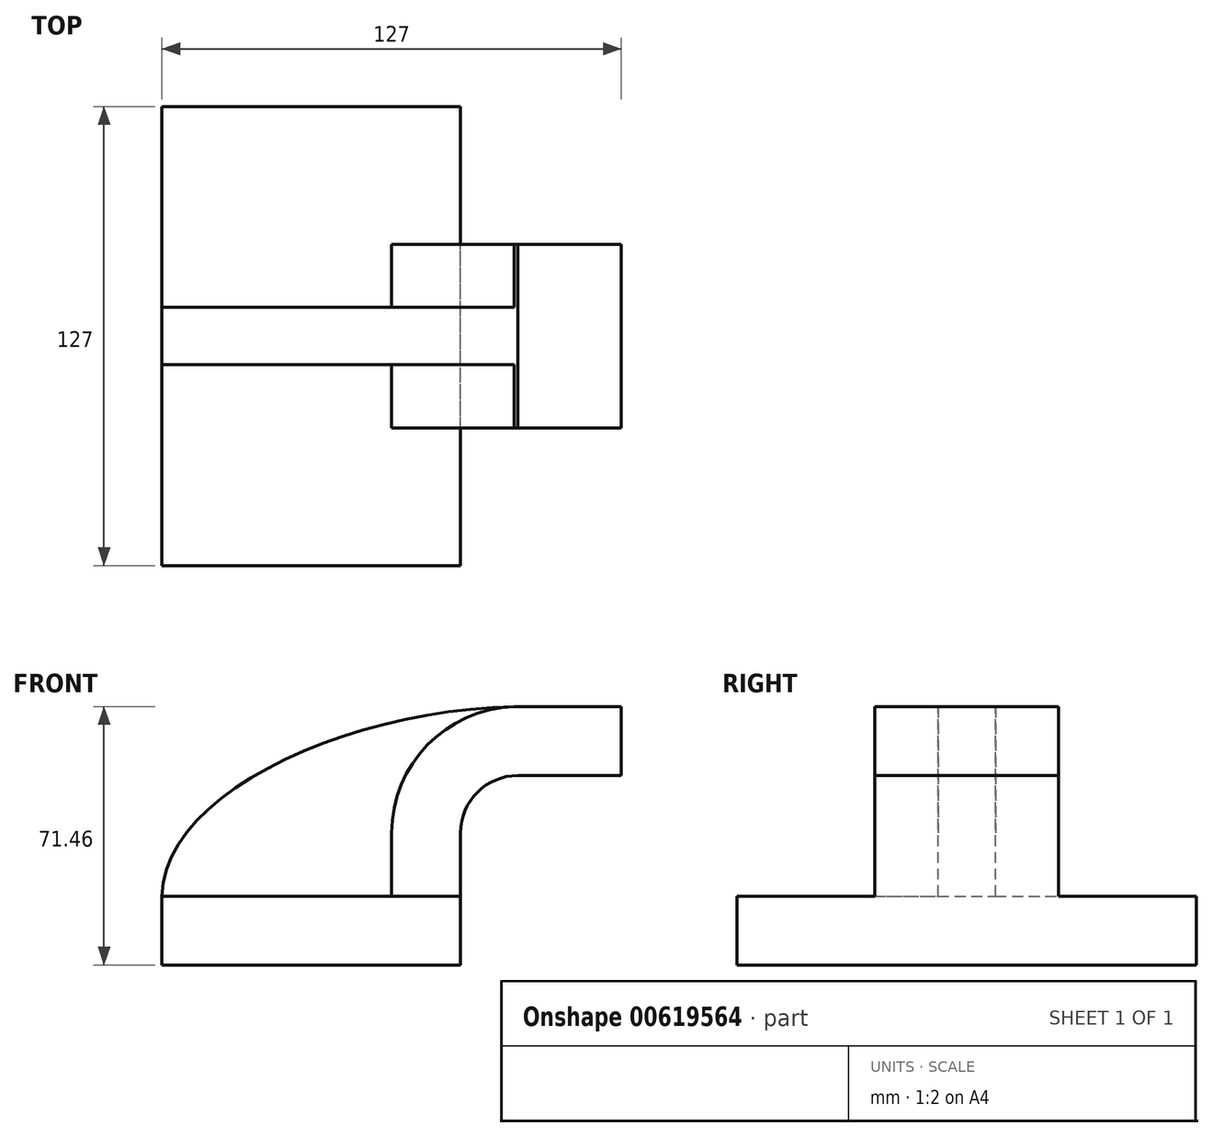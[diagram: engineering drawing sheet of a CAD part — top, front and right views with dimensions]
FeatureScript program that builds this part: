
annotation { "Feature Type Name" : "Feature", "Feature Type Description" : "" }
export const myFeature = defineFeature(function(context is Context, id is Id, definition is map)
    precondition{}
    {
        {
            var Q0;
            Q0=qCreatedBy(makeId("Front.planeOp"),FACE);
            var sketch = newSketch(context, id + "F0", { "sketchPlane" : qUnion([Q0])});
            skLineSegment(sketch, "E0.bottom", {"start": v(-41.28, -9.53) * mm, "end": v(41.28, -9.53) * mm});
            skLineSegment(sketch, "E0.top", {"start": v(-41.28, 9.53) * mm, "end": v(41.28, 9.53) * mm});
            skLineSegment(sketch, "E0.left", {"start": v(-41.28, -9.53) * mm, "end": v(-41.28, 9.53) * mm});
            skLineSegment(sketch, "E0.right", {"start": v(41.28, -9.53) * mm, "end": v(41.28, 9.53) * mm});
            skPoint(sketch, "E0.middle", {"position": v(0, 0) * mm});
            skLineSegment(sketch, "E1.bottom", {"start": v(60.32, 66.67) * mm, "end": v(111.12, 66.67) * mm});
            skLineSegment(sketch, "E1.top", {"start": v(60.32, 38.1) * mm, "end": v(111.12, 38.1) * mm});
            skLineSegment(sketch, "E1.left", {"start": v(60.32, 66.67) * mm, "end": v(60.32, 38.1) * mm});
            skLineSegment(sketch, "E1.right", {"start": v(111.12, 66.67) * mm, "end": v(111.12, 38.1) * mm});
            skPoint(sketch, "E1.middle", {"position": v(85.72, 52.39) * mm});
            skLineSegment(sketch, "E2", {"start": v(41.28, 9.53) * mm, "end": v(41.28, 27) * mm});
            skArc(sketch, "E3", {"start": v(41.28, 27) * mm, "mid": v(45.92, 38.23) * mm, "end": v(57.15, 42.88) * mm});
            skLineSegment(sketch, "E4", {"start": v(57.15, 42.88) * mm, "end": v(85.72, 42.88) * mm});
            skPoint(sketch, "E4.endSnap0", {"position": v(85.72, 38.1) * mm});
            skLineSegment(sketch, "E5.0", {"start": v(57.15, 61.93) * mm, "end": v(85.72, 61.93) * mm});
            skArc(sketch, "E5.1", {"start": v(22.23, 27) * mm, "mid": v(32.45, 51.7) * mm, "end": v(57.15, 61.93) * mm});
            skLineSegment(sketch, "E5.2", {"start": v(22.23, 9.53) * mm, "end": v(22.23, 27) * mm});
            skLineSegment(sketch, "E6", {"start": v(85.72, 42.88) * mm, "end": v(85.72, 66.67) * mm});
            skFitSpline(sketch, "E7", {"points": [v(-41.28, 9.53) * mm, v(57.15, 61.93) * mm], "startDerivative": vector(1.35, 85.95) * mm, "endDerivative": vector(139.55, 1.51) * mm});
            skSolve(sketch);
        }
        {
            var Q0;
            Q0=makeQuery(id+"F0.imprint","IMPRINT",FACE,{"disambiguationData":[TD([[makeQuery(id+"F0.imprint","IMPRINT",EDGE,{"derivedFrom":sQuery(id+"F0.wireOp",EDGE,"E0.bottom")}),1.0]])]});
            extrude(context, id + "F1", {"entities" : qUnion([Q0]), "endBound" : BoundingType.SYMMETRIC, "depth" : 127 * mm, "offsetDistance" : 25.4 * mm});
        }
        {
            var Q0;
            {var subQ1=sQuery(id+"F0.wireOp",EDGE,"E2");Q0=makeQuery(id+"F0.imprint","IMPRINT",FACE,{"disambiguationData":[TD([[makeQuery(id+"F0.imprint","IMPRINT",EDGE,{"derivedFrom":subQ1}),1.0]])]});}
            var Q1;
            {var subQ0=sQuery(id+"F0.wireOp",EDGE,"E5.0");var subQ1=sQuery(id+"F0.wireOp",EDGE,"E1.left");var subQ2=makeQuery(id+"F0.imprint","INTERSECT",VERTEX,{"derivedFrom":[subQ1,subQ0]});Q1=makeQuery(id+"F0.imprint","IMPRINT",FACE,{"disambiguationData":[TD([[makeQuery(id+"F0.imprint","IMPRINT",EDGE,{"disambiguationData":[TD([[subQ2,-1.0]])],"derivedFrom":subQ1}),1.0]])]});}
            extrude(context, id + "F2", {"entities" : qUnion([Q0, Q1]), "operationType" : NewBodyOperationType.ADD, "endBound" : BoundingType.SYMMETRIC, "depth" : 50.8 * mm, "offsetDistance" : 25.4 * mm});
        }
        {
            var Q0;
            {var subQ3=sQuery(id+"F0.wireOp",EDGE,"E5.2");Q0=makeQuery(id+"F0.imprint","IMPRINT",FACE,{"disambiguationData":[TD([[makeQuery(id+"F0.imprint","IMPRINT",EDGE,{"derivedFrom":subQ3}),1.0]])]});}
            extrude(context, id + "F3", {"entities" : qUnion([Q0]), "operationType" : NewBodyOperationType.ADD, "endBound" : BoundingType.SYMMETRIC, "depth" : 15.88 * mm, "offsetDistance" : 25.4 * mm});
        }
    });
